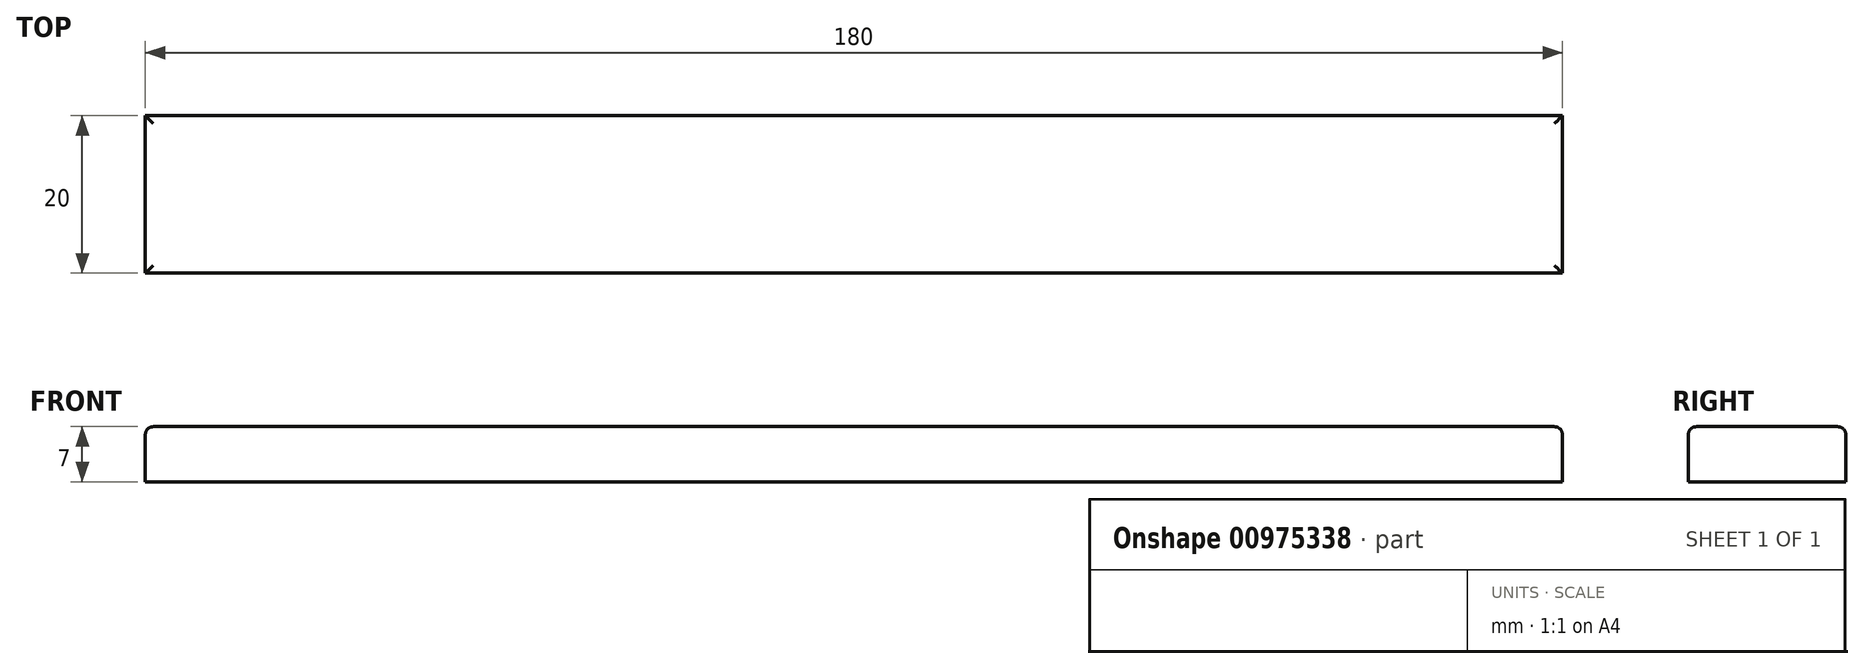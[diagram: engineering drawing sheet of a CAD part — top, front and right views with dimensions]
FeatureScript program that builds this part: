
annotation { "Feature Type Name" : "Feature", "Feature Type Description" : "" }
export const myFeature = defineFeature(function(context is Context, id is Id, definition is map)
    precondition{}
    {
        {
            var Q0;
            Q0=qCreatedBy(makeId("Top.planeOp"),FACE);
            var sketch = newSketch(context, id + "F0", { "sketchPlane" : qUnion([Q0])});
            skLineSegment(sketch, "E0.bottom", {"start": v(0, 0) * mm, "end": v(180, 0) * mm});
            skLineSegment(sketch, "E0.top", {"start": v(0, 20) * mm, "end": v(180, 20) * mm});
            skLineSegment(sketch, "E0.left", {"start": v(0, 0) * mm, "end": v(0, 20) * mm});
            skLineSegment(sketch, "E0.right", {"start": v(180, 0) * mm, "end": v(180, 20) * mm});
            skSolve(sketch);
        }
        {
            var Q0;
            Q0=makeQuery(id+"F0.imprint","IMPRINT",FACE,{"disambiguationData":[TD([[makeQuery(id+"F0.imprint","IMPRINT",EDGE,{"derivedFrom":sQuery(id+"F0.wireOp",EDGE,"E0.bottom")}),1.0]])]});
            extrude(context, id + "F1", {"entities" : qUnion([Q0]), "oppositeDirection" : true, "depth" : 7 * mm, "offsetDistance" : 25 * mm});
        }
        {
            var Q0;
            Q0=makeQuery(id+"F1.opExtrude","CAP_EDGE",EDGE,{"disambiguationData":[OSD([sQuery(id+"F0.wireOp",EDGE,"E0.top")])],"isStart":true});
            var Q1;
            Q1=makeQuery(id+"F1.opExtrude","CAP_EDGE",EDGE,{"disambiguationData":[OSD([sQuery(id+"F0.wireOp",EDGE,"E0.left")])],"isStart":true});
            var Q2;
            Q2=makeQuery(id+"F1.opExtrude","CAP_EDGE",EDGE,{"disambiguationData":[OSD([sQuery(id+"F0.wireOp",EDGE,"E0.bottom")])],"isStart":true});
            var Q3;
            Q3=makeQuery(id+"F1.opExtrude","CAP_EDGE",EDGE,{"disambiguationData":[OSD([sQuery(id+"F0.wireOp",EDGE,"E0.right")])],"isStart":true});
            fillet(context, id + "F2", {"entities" : qUnion([Q0, Q1, Q2, Q3]), "radius" : 1 * mm, "tangentPropagation" : true, "allowEdgeOverflow" : false});
        }
    });
